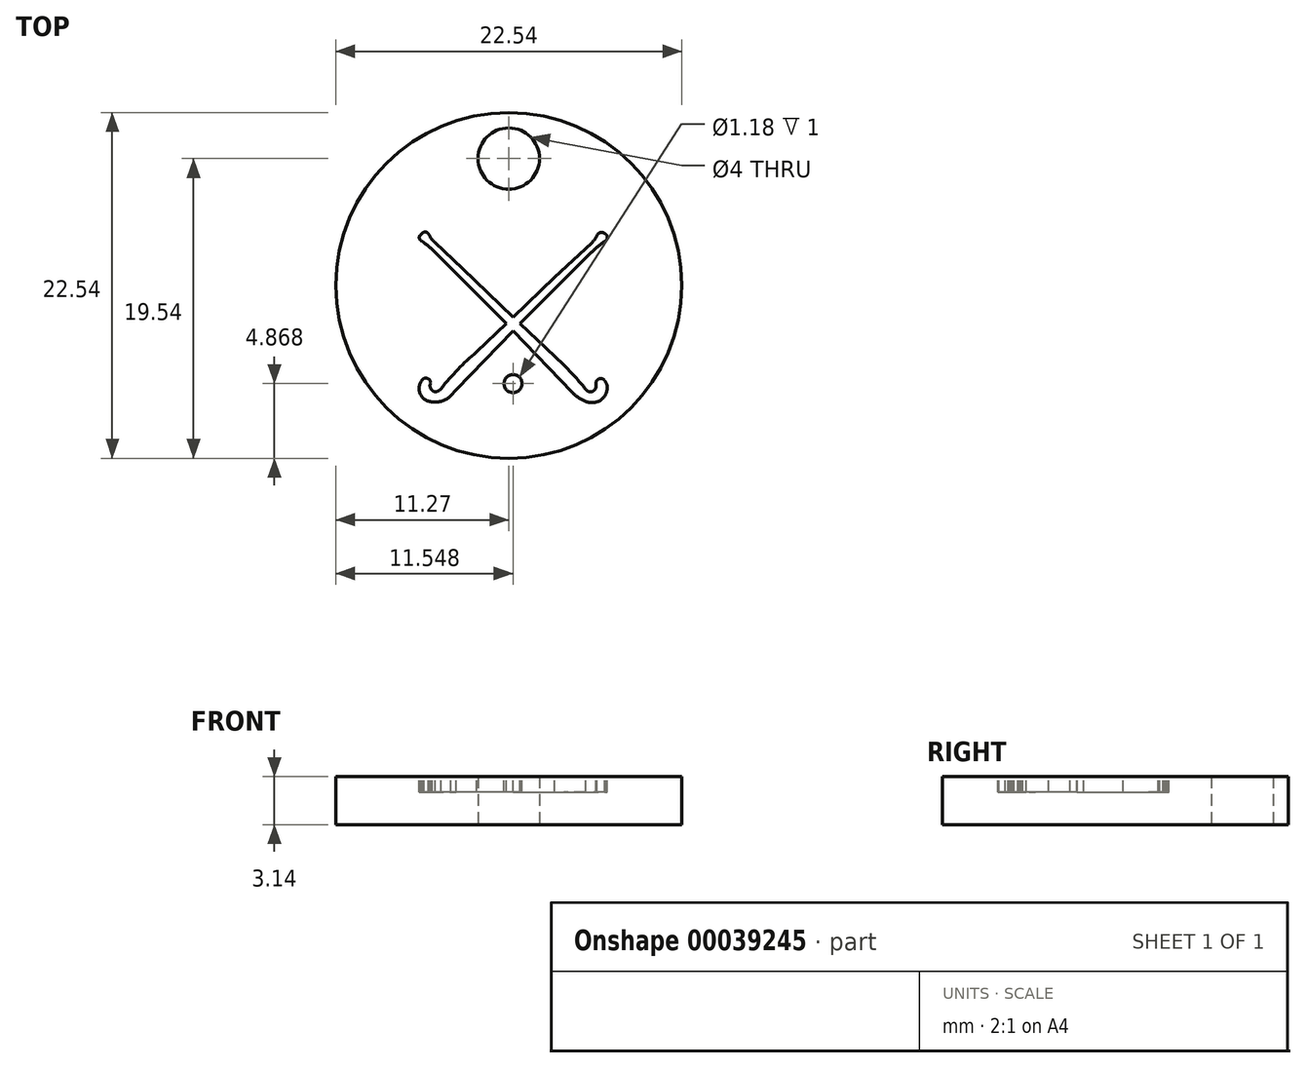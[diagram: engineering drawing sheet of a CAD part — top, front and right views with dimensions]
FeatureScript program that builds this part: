
annotation { "Feature Type Name" : "Feature", "Feature Type Description" : "" }
export const myFeature = defineFeature(function(context is Context, id is Id, definition is map)
    precondition{}
    {
        {
            var Q0;
            Q0=qCreatedBy(makeId("Top.planeOp"),FACE);
            var sketch = newSketch(context, id + "F0", { "sketchPlane" : qUnion([Q0])});
            skCircle(sketch, "E0", {"center": v(0, 0) * mm, "radius": 11.27 * mm});
            skPoint(sketch, "E1", {"position": v(0, 8.27) * mm});
            skPoint(sketch, "E2", {"position": v(0, -5.5) * mm});
            skSolve(sketch);
        }
        {
            var Q0;
            Q0=makeQuery(id+"F0.imprint","IMPRINT",FACE,{"disambiguationData":[TD([[makeQuery(id+"F0.imprint","IMPRINT",EDGE,{"derivedFrom":sQuery(id+"F0.wireOp",EDGE,"E0")}),1.0]])]});
            extrude(context, id + "F1", {"entities" : qUnion([Q0]), "depth" : 3.14 * mm});
        }
        {
            var Q0;
            Q0=makeQuery(id+"F1.opExtrude","CAP_FACE",FACE,{"disambiguationData":[OSD([sQuery(id+"F0.wireOp",EDGE,"E0"),sQuery(id+"F0.wireOp",EDGE,"b1e43adf-e12e-4730-8375-2b69b1993464")])],"isStart":false});
            var sketch = newSketch(context, id + "F2", { "sketchPlane" : qUnion([Q0])});
            skLineSegment(sketch, "E3", {"start": v(-58.03, 25.26) * mm, "end": v(-61.73, 21.4) * mm});
            skLineSegment(sketch, "E4", {"start": v(-58.03, 25.26) * mm, "end": v(-54.19, 21.25) * mm});
            skArc(sketch, "E5", {"start": v(-63.92, 22.09) * mm, "mid": v(-64.08, 21.16) * mm, "end": v(-63.3, 20.62) * mm});
            skArc(sketch, "E6", {"start": v(-63.4, 21.85) * mm, "mid": v(-63.59, 22.14) * mm, "end": v(-63.92, 22.09) * mm});
            skArc(sketch, "E7", {"start": v(-63.4, 21.85) * mm, "mid": v(-63.4, 21.48) * mm, "end": v(-63.09, 21.27) * mm});
            skArc(sketch, "E8", {"start": v(-63.09, 21.27) * mm, "mid": v(-62.89, 21.35) * mm, "end": v(-62.71, 21.48) * mm});
            skArc(sketch, "E9", {"start": v(-63.3, 20.62) * mm, "mid": v(-62.65, 20.67) * mm, "end": v(-62.1, 21.03) * mm});
            skLineSegment(sketch, "E10", {"start": v(-62.1, 21.03) * mm, "end": v(-61.73, 21.4) * mm});
            skLineSegment(sketch, "E11", {"start": v(-58.48, 25.72) * mm, "end": v(-60.4, 23.87) * mm});
            skArc(sketch, "E12", {"start": v(-60.4, 23.87) * mm, "mid": v(-61.63, 22.74) * mm, "end": v(-62.71, 21.48) * mm});
            skLineSegment(sketch, "E13", {"start": v(-58.48, 25.72) * mm, "end": v(-62.95, 30.21) * mm});
            skLineSegment(sketch, "E14", {"start": v(-58.02, 26.13) * mm, "end": v(-55.3, 28.73) * mm});
            skLineSegment(sketch, "E15", {"start": v(-58.02, 26.13) * mm, "end": v(-61.34, 29.3) * mm});
            skLineSegment(sketch, "E16", {"start": v(-57.56, 25.71) * mm, "end": v(-54.53, 28.76) * mm});
            skLineSegment(sketch, "E17", {"start": v(-57.56, 25.71) * mm, "end": v(-54.73, 23.01) * mm});
            skLineSegment(sketch, "E18", {"start": v(-55.3, 28.73) * mm, "end": v(-52.9, 30.98) * mm});
            skLineSegment(sketch, "E19", {"start": v(-54.53, 28.76) * mm, "end": v(-52.93, 30.36) * mm});
            skArc(sketch, "E20", {"start": v(-52.9, 30.98) * mm, "mid": v(-52.72, 31.2) * mm, "end": v(-52.58, 31.44) * mm});
            skArc(sketch, "E21", {"start": v(-52.03, 31.1) * mm, "mid": v(-52.5, 30.75) * mm, "end": v(-52.93, 30.36) * mm});
            skArc(sketch, "E22", {"start": v(-52.03, 31.1) * mm, "mid": v(-51.88, 31.33) * mm, "end": v(-52.03, 31.57) * mm});
            skArc(sketch, "E23", {"start": v(-52.03, 31.57) * mm, "mid": v(-52.34, 31.65) * mm, "end": v(-52.58, 31.44) * mm});
            skLineSegment(sketch, "E24", {"start": v(-61.34, 29.3) * mm, "end": v(-63.11, 31) * mm});
            skLineSegment(sketch, "E25", {"start": v(-62.95, 30.21) * mm, "end": v(-63.16, 30.42) * mm});
            skArc(sketch, "E26", {"start": v(-63.16, 30.42) * mm, "mid": v(-63.49, 30.72) * mm, "end": v(-63.85, 30.99) * mm});
            skArc(sketch, "E27", {"start": v(-64.06, 31.52) * mm, "mid": v(-64.14, 31.3) * mm, "end": v(-64, 31.11) * mm});
            skArc(sketch, "E28", {"start": v(-63.56, 31.59) * mm, "mid": v(-63.74, 31.7) * mm, "end": v(-63.93, 31.62) * mm});
            skLineSegment(sketch, "E29", {"start": v(-63.93, 31.62) * mm, "end": v(-64.06, 31.52) * mm});
            skLineSegment(sketch, "E30", {"start": v(-64, 31.11) * mm, "end": v(-63.85, 30.99) * mm});
            skArc(sketch, "E31", {"start": v(-63.41, 31.32) * mm, "mid": v(-63.47, 31.46) * mm, "end": v(-63.56, 31.59) * mm});
            skArc(sketch, "E32", {"start": v(-63.41, 31.32) * mm, "mid": v(-63.27, 31.15) * mm, "end": v(-63.11, 31) * mm});
            skArc(sketch, "E33", {"start": v(-52.04, 21.98) * mm, "mid": v(-52.39, 22.14) * mm, "end": v(-52.63, 21.85) * mm});
            skArc(sketch, "E34", {"start": v(-53.3, 21.44) * mm, "mid": v(-52.9, 21.28) * mm, "end": v(-52.63, 21.6) * mm});
            skArc(sketch, "E35", {"start": v(-53.21, 20.62) * mm, "mid": v(-52.3, 20.75) * mm, "end": v(-51.89, 21.57) * mm});
            skArc(sketch, "E36", {"start": v(-51.89, 21.57) * mm, "mid": v(-51.93, 21.8) * mm, "end": v(-52.04, 21.98) * mm});
            skArc(sketch, "E37", {"start": v(-54.19, 21.25) * mm, "mid": v(-53.74, 20.88) * mm, "end": v(-53.21, 20.62) * mm});
            skArc(sketch, "E38", {"start": v(-53.3, 21.44) * mm, "mid": v(-53.99, 22.25) * mm, "end": v(-54.73, 23.01) * mm});
            skLineSegment(sketch, "E39", {"start": v(-52.63, 21.85) * mm, "end": v(-52.63, 21.6) * mm});
            skLineSegment(sketch, "E40", {"start": v(0.28, -2.96) * mm, "end": v(-3.42, -6.82) * mm});
            skLineSegment(sketch, "E41", {"start": v(0.28, -2.96) * mm, "end": v(4.12, -6.96) * mm});
            skArc(sketch, "E42", {"start": v(-5.61, -6.13) * mm, "mid": v(-5.78, -7.06) * mm, "end": v(-5, -7.59) * mm});
            skArc(sketch, "E43", {"start": v(-5.1, -6.36) * mm, "mid": v(-5.28, -6.07) * mm, "end": v(-5.61, -6.13) * mm});
            skArc(sketch, "E44", {"start": v(-5.1, -6.36) * mm, "mid": v(-5.08, -6.73) * mm, "end": v(-4.78, -6.94) * mm});
            skArc(sketch, "E45", {"start": v(-4.78, -6.94) * mm, "mid": v(-4.58, -6.87) * mm, "end": v(-4.4, -6.74) * mm});
            skArc(sketch, "E46", {"start": v(-5, -7.59) * mm, "mid": v(-4.34, -7.54) * mm, "end": v(-3.79, -7.18) * mm});
            skLineSegment(sketch, "E47", {"start": v(-3.79, -7.18) * mm, "end": v(-3.42, -6.82) * mm});
            skLineSegment(sketch, "E48", {"start": v(-0.17, -2.49) * mm, "end": v(-2.1, -4.34) * mm});
            skArc(sketch, "E49", {"start": v(-2.1, -4.34) * mm, "mid": v(-3.32, -5.47) * mm, "end": v(-4.4, -6.74) * mm});
            skLineSegment(sketch, "E50", {"start": v(-0.17, -2.49) * mm, "end": v(-4.64, 2) * mm});
            skLineSegment(sketch, "E51", {"start": v(0.3, -2.08) * mm, "end": v(3, 0.52) * mm});
            skLineSegment(sketch, "E52", {"start": v(0.3, -2.08) * mm, "end": v(-3.03, 1.09) * mm});
            skLineSegment(sketch, "E53", {"start": v(0.74, -2.5) * mm, "end": v(3.78, 0.55) * mm});
            skLineSegment(sketch, "E54", {"start": v(0.74, -2.5) * mm, "end": v(3.57, -5.2) * mm});
            skLineSegment(sketch, "E55", {"start": v(3, 0.52) * mm, "end": v(5.4, 2.76) * mm});
            skLineSegment(sketch, "E56", {"start": v(3.78, 0.55) * mm, "end": v(5.38, 2.14) * mm});
            skArc(sketch, "E57", {"start": v(5.4, 2.76) * mm, "mid": v(5.59, 2.98) * mm, "end": v(5.73, 3.23) * mm});
            skArc(sketch, "E58", {"start": v(6.28, 2.88) * mm, "mid": v(5.8, 2.54) * mm, "end": v(5.38, 2.14) * mm});
            skArc(sketch, "E59", {"start": v(6.28, 2.88) * mm, "mid": v(6.43, 3.12) * mm, "end": v(6.28, 3.36) * mm});
            skArc(sketch, "E60", {"start": v(6.28, 3.36) * mm, "mid": v(5.97, 3.44) * mm, "end": v(5.73, 3.23) * mm});
            skLineSegment(sketch, "E61", {"start": v(-3.03, 1.09) * mm, "end": v(-4.8, 2.78) * mm});
            skLineSegment(sketch, "E62", {"start": v(-4.64, 2) * mm, "end": v(-4.85, 2.21) * mm});
            skArc(sketch, "E63", {"start": v(-4.85, 2.21) * mm, "mid": v(-5.18, 2.51) * mm, "end": v(-5.54, 2.78) * mm});
            skArc(sketch, "E64", {"start": v(-5.75, 3.3) * mm, "mid": v(-5.83, 3.09) * mm, "end": v(-5.7, 2.9) * mm});
            skArc(sketch, "E65", {"start": v(-5.25, 3.38) * mm, "mid": v(-5.43, 3.48) * mm, "end": v(-5.63, 3.4) * mm});
            skLineSegment(sketch, "E66", {"start": v(-5.63, 3.4) * mm, "end": v(-5.75, 3.3) * mm});
            skLineSegment(sketch, "E67", {"start": v(-5.7, 2.9) * mm, "end": v(-5.54, 2.78) * mm});
            skArc(sketch, "E68", {"start": v(-5.1, 3.11) * mm, "mid": v(-5.16, 3.25) * mm, "end": v(-5.25, 3.38) * mm});
            skArc(sketch, "E69", {"start": v(-5.1, 3.11) * mm, "mid": v(-4.96, 2.94) * mm, "end": v(-4.8, 2.78) * mm});
            skArc(sketch, "E70", {"start": v(6.26, -6.23) * mm, "mid": v(5.92, -6.08) * mm, "end": v(5.68, -6.36) * mm});
            skArc(sketch, "E71", {"start": v(5.01, -6.77) * mm, "mid": v(5.4, -6.93) * mm, "end": v(5.68, -6.6) * mm});
            skArc(sketch, "E72", {"start": v(5.1, -7.59) * mm, "mid": v(6, -7.46) * mm, "end": v(6.42, -6.64) * mm});
            skArc(sketch, "E73", {"start": v(6.42, -6.64) * mm, "mid": v(6.38, -6.42) * mm, "end": v(6.26, -6.23) * mm});
            skArc(sketch, "E74", {"start": v(4.12, -6.96) * mm, "mid": v(4.57, -7.33) * mm, "end": v(5.1, -7.59) * mm});
            skArc(sketch, "E75", {"start": v(5.01, -6.77) * mm, "mid": v(4.32, -5.96) * mm, "end": v(3.57, -5.2) * mm});
            skLineSegment(sketch, "E76", {"start": v(5.68, -6.36) * mm, "end": v(5.68, -6.6) * mm});
            skCircle(sketch, "E77", {"center": v(0.28, -6.4) * mm, "radius": 0.59 * mm});
            skSolve(sketch);
        }
        {
            var Q0;
            Q0=qSketchRegion(id+"F2",true);
            extrude(context, id + "F3", {"entities" : qUnion([Q0]), "operationType" : NewBodyOperationType.REMOVE, "oppositeDirection" : true, "depth" : 1 * mm});
        }
        {
            var Q0;
            Q0=sQuery(id+"F0.wireOp",VERTEX,"E1");
            var Q1;
            Q1=makeQuery(id+"F1.opExtrude","SWEPT_BODY",BODY,{"disambiguationData":[OSD([sQuery(id+"F0.wireOp",EDGE,"E0")])]});
            hole(context, id + "F4", {"style" : HoleStyle.SIMPLE, "endStyle" : HoleEndStyle.THROUGH, "oppositeDirection" : true, "holeDiameter" : 4 * mm, "locations" : qUnion([Q0]), "scope" : qUnion([Q1]), "isTappedThrough" : true});
        }
    });
